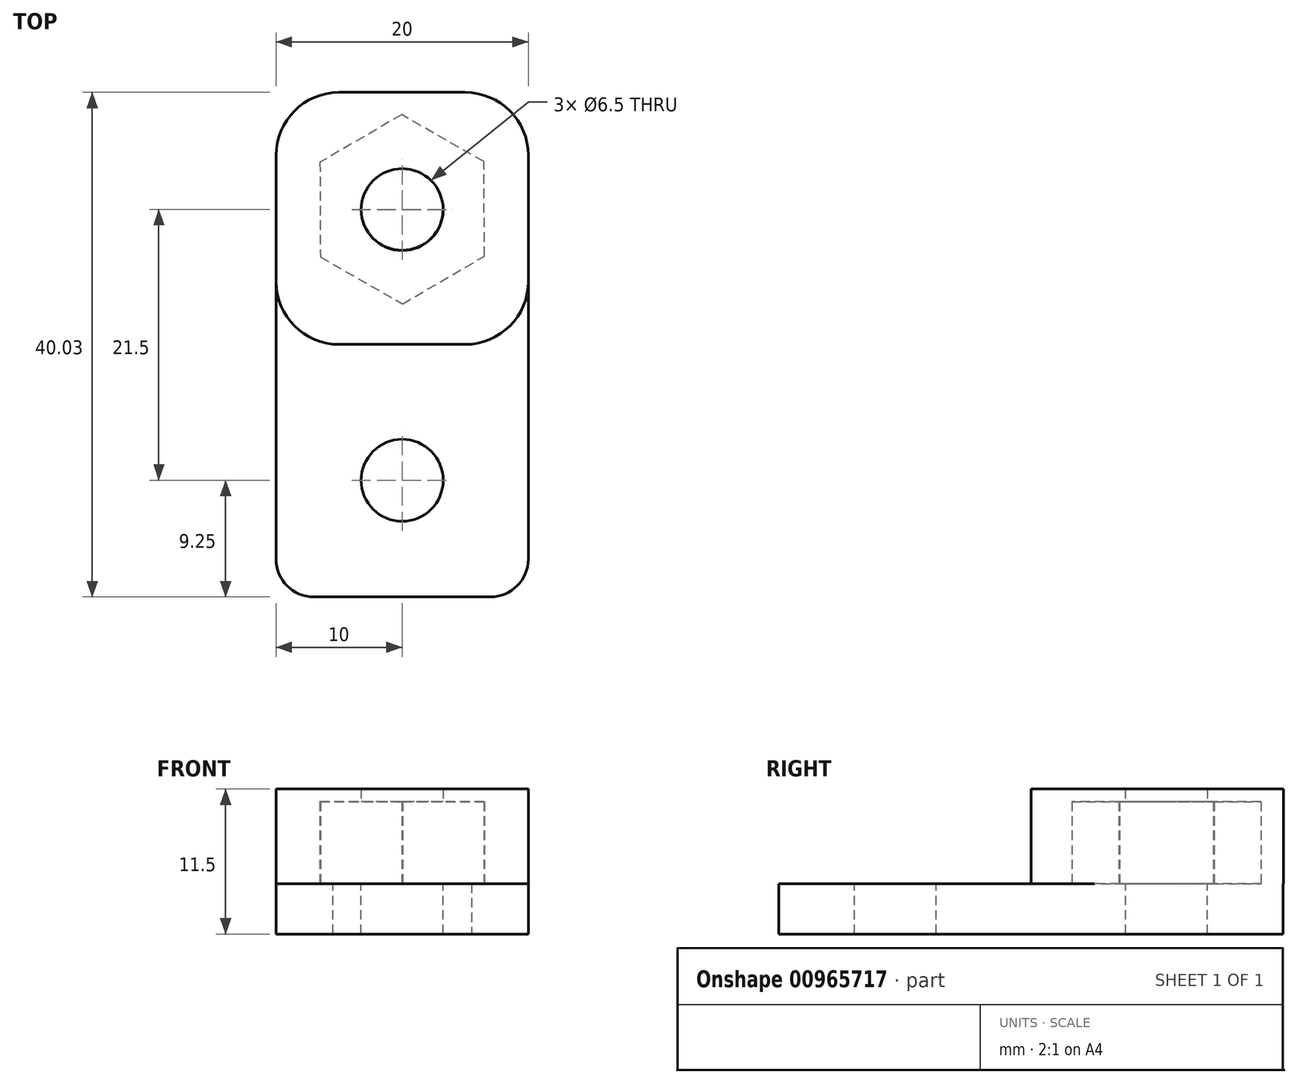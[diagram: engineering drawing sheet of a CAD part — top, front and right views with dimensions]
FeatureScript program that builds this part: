
annotation { "Feature Type Name" : "Feature", "Feature Type Description" : "" }
export const myFeature = defineFeature(function(context is Context, id is Id, definition is map)
    precondition{}
    {
        {
            var Q0;
            Q0=qCreatedBy(makeId("Top.planeOp"),FACE);
            var sketch = newSketch(context, id + "F0", { "sketchPlane" : qUnion([Q0])});
            skLineSegment(sketch, "E0.bottom", {"start": v(0, 0) * mm, "end": v(20, 0) * mm});
            skLineSegment(sketch, "E0.top", {"start": v(0, 40) * mm, "end": v(20, 40) * mm});
            skLineSegment(sketch, "E0.left", {"start": v(0, 0) * mm, "end": v(0, 40) * mm});
            skLineSegment(sketch, "E0.right", {"start": v(20, 0) * mm, "end": v(20, 40) * mm});
            skLineSegment(sketch, "E1.left", {"start": v(0, 40) * mm, "end": v(0, 40) * mm});
            skLineSegment(sketch, "E1.right", {"start": v(20, 40) * mm, "end": v(20, 40) * mm});
            skSolve(sketch);
        }
        {
            var Q0;
            Q0=makeQuery(id+"F0.imprint","IMPRINT",FACE,{"disambiguationData":[TD([[makeQuery(id+"F0.imprint","IMPRINT",EDGE,{"derivedFrom":sQuery(id+"F0.wireOp",EDGE,"E0.bottom")}),1.0]])]});
            extrude(context, id + "F1", {"entities" : qUnion([Q0]), "depth" : 4 * mm, "offsetDistance" : 25 * mm});
        }
        {
            var Q0;
            Q0=makeQuery(id+"F1.opExtrude","SWEPT_EDGE",EDGE,{"disambiguationData":[OSD([sQuery(id+"F0.wireOp",EDGE,"E0.right"),sQuery(id+"F0.wireOp",EDGE,"E0.top")])]});
            var Q1;
            Q1=makeQuery(id+"F1.opExtrude","SWEPT_EDGE",EDGE,{"disambiguationData":[OSD([sQuery(id+"F0.wireOp",EDGE,"E0.bottom"),sQuery(id+"F0.wireOp",EDGE,"E0.right")])]});
            var Q2;
            Q2=makeQuery(id+"F1.opExtrude","SWEPT_EDGE",EDGE,{"disambiguationData":[OSD([sQuery(id+"F0.wireOp",EDGE,"E0.left"),sQuery(id+"F0.wireOp",EDGE,"E0.top")])]});
            var Q3;
            Q3=makeQuery(id+"F1.opExtrude","SWEPT_EDGE",EDGE,{"disambiguationData":[OSD([sQuery(id+"F0.wireOp",EDGE,"E0.bottom"),sQuery(id+"F0.wireOp",EDGE,"E0.left")])]});
            fillet(context, id + "F2", {"entities" : qUnion([Q0, Q1, Q2, Q3]), "radius" : 3 * mm, "tangentPropagation" : true, "allowEdgeOverflow" : false});
        }
        {
            var Q0;
            Q0=makeQuery(id+"F1.opExtrude","CAP_FACE",FACE,{"disambiguationData":[OSD([sQuery(id+"F0.wireOp",EDGE,"E0.bottom"),sQuery(id+"F0.wireOp",EDGE,"E0.left"),sQuery(id+"F0.wireOp",EDGE,"E0.right"),sQuery(id+"F0.wireOp",EDGE,"E0.top")])],"isStart":false});
            var sketch = newSketch(context, id + "F3", { "sketchPlane" : qUnion([Q0])});
            skLineSegment(sketch, "E2", {"start": v(0, 20) * mm, "end": v(20, 20) * mm, "construction": true});
            skCircle(sketch, "E3", {"center": v(10, 30.75) * mm, "radius": 3.25 * mm});
            skPoint(sketch, "E3.centerSnap0", {"position": v(10, 40) * mm});
            skCircle(sketch, "E4", {"center": v(10, 9.25) * mm, "radius": 3.25 * mm});
            skPoint(sketch, "E4.centerSnap0", {"position": v(10, 0) * mm});
            skSolve(sketch);
        }
        {
            var Q0;
            Q0=makeQuery(id+"F3.imprint","IMPRINT",FACE,{"disambiguationData":[TD([[makeQuery(id+"F3.imprint","IMPRINT",EDGE,{"derivedFrom":sQuery(id+"F3.wireOp",EDGE,"E3")}),1.0]])]});
            var Q1;
            Q1=makeQuery(id+"F3.imprint","IMPRINT",FACE,{"disambiguationData":[TD([[makeQuery(id+"F3.imprint","IMPRINT",EDGE,{"derivedFrom":sQuery(id+"F3.wireOp",EDGE,"E4")}),1.0]])]});
            var Q2;
            Q2=sQuery(id+"F3.wireOp",EDGE,"E3");
            var Q3;
            Q3=sQuery(id+"F3.wireOp",EDGE,"E4");
            extrude(context, id + "F4", {"entities" : qUnion([Q0, Q1]), "operationType" : NewBodyOperationType.REMOVE, "surfaceEntities" : qUnion([Q2, Q3]), "endBound" : BoundingType.THROUGH_ALL, "oppositeDirection" : true, "depth" : 4 * mm, "offsetDistance" : 25 * mm});
        }
        {
            var Q0;
            Q0=makeQuery(id+"F1.opExtrude","CAP_FACE",FACE,{"disambiguationData":[OSD([sQuery(id+"F0.wireOp",EDGE,"E0.bottom"),sQuery(id+"F0.wireOp",EDGE,"E0.left"),sQuery(id+"F0.wireOp",EDGE,"E0.right"),sQuery(id+"F0.wireOp",EDGE,"E0.top")])],"isStart":false});
            var sketch = newSketch(context, id + "F5", { "sketchPlane" : qUnion([Q0])});
            skCircle(sketch, "E5.cCircle", {"center": v(10, 30.75) * mm, "radius": 7.5 * mm, "construction": true});
            skLineSegment(sketch, "E5.0", {"start": v(10.03, 23.24) * mm, "end": v(3.52, 26.97) * mm});
            skLineSegment(sketch, "E5.1", {"start": v(3.52, 26.97) * mm, "end": v(3.48, 34.47) * mm});
            skLineSegment(sketch, "E5.2", {"start": v(3.48, 34.47) * mm, "end": v(9.97, 38.26) * mm});
            skLineSegment(sketch, "E5.3", {"start": v(9.97, 38.26) * mm, "end": v(16.48, 34.53) * mm});
            skLineSegment(sketch, "E5.4", {"start": v(16.48, 34.53) * mm, "end": v(16.52, 27.03) * mm});
            skLineSegment(sketch, "E5.5", {"start": v(16.52, 27.03) * mm, "end": v(10.03, 23.24) * mm});
            skSolve(sketch);
        }
        {
            var Q0;
            Q0=makeQuery(id+"F5.imprint","IMPRINT",FACE,{"disambiguationData":[TD([[makeQuery(id+"F5.imprint","IMPRINT",EDGE,{"derivedFrom":sQuery(id+"F5.wireOp",EDGE,"E5.0")}),1.0]])]});
            var sketch = newSketch(context, id + "F6", { "sketchPlane" : qUnion([Q0])});
            skLineSegment(sketch, "E6.bottom", {"start": v(20, 20.03) * mm, "end": v(0, 20.03) * mm});
            skLineSegment(sketch, "E6.top", {"start": v(20, 40.03) * mm, "end": v(0, 40.03) * mm});
            skLineSegment(sketch, "E6.left", {"start": v(20, 20.03) * mm, "end": v(20, 40.03) * mm});
            skLineSegment(sketch, "E6.right", {"start": v(0, 20.03) * mm, "end": v(0, 40.03) * mm});
            skSolve(sketch);
        }
        {
            var Q0;
            Q0=makeQuery(id+"F6.imprint","IMPRINT",FACE,{"disambiguationData":[TD([[makeQuery(id+"F6.imprint","IMPRINT",EDGE,{"derivedFrom":makeQuery(id+"F5.imprint","IMPRINT",EDGE,{"derivedFrom":sQuery(id+"F5.wireOp",EDGE,"E5.0")})}),-1.0]])]});
            var Q1;
            {var subQ6=sQuery(id+"F6.wireOp",EDGE,"E6.top");Q1=makeQuery(id+"F6.imprint","IMPRINT",FACE,{"disambiguationData":[TD([[makeQuery(id+"F6.imprint","IMPRINT",EDGE,{"derivedFrom":subQ6}),1.0]])]});}
            var Q2;
            {var subQ5=sQuery(id+"F6.wireOp",EDGE,"E6.bottom");Q2=makeQuery(id+"F6.imprint","IMPRINT",FACE,{"disambiguationData":[TD([[makeQuery(id+"F6.imprint","IMPRINT",EDGE,{"derivedFrom":subQ5}),-1.0]])]});}
            extrude(context, id + "F7", {"entities" : qUnion([Q0, Q1, Q2]), "operationType" : NewBodyOperationType.ADD, "depth" : 6.5 * mm, "offsetDistance" : 25 * mm});
        }
        {
            var Q0;
            Q0 = qSketchRegion(id + "F5", true);
            var Q1;
            Q1=sQuery(id+"F5.wireOp",EDGE,"E5.0");
            var Q2;
            Q2=sQuery(id+"F5.wireOp",EDGE,"E5.2");
            var Q3;
            Q3=sQuery(id+"F5.wireOp",EDGE,"E5.1");
            var Q4;
            Q4=sQuery(id+"F5.wireOp",EDGE,"E5.3");
            var Q5;
            Q5=sQuery(id+"F5.wireOp",EDGE,"E5.5");
            var Q6;
            Q6=sQuery(id+"F5.wireOp",EDGE,"E5.4");
            extrude(context, id + "F8", {"entities" : qUnion([Q0]), "operationType" : NewBodyOperationType.REMOVE, "surfaceEntities" : qUnion([Q1, Q2, Q3, Q4, Q5, Q6]), "depth" : 6.6 * mm, "offsetDistance" : 25 * mm});
        }
        {
            var Q0;
            Q0=makeQuery(id+"F7.opExtrude","SWEPT_EDGE",EDGE,{"disambiguationData":[OSD([sQuery(id+"F6.wireOp",EDGE,"E6.top"),sQuery(id+"F6.wireOp",EDGE,"E6.left")])]});
            var Q1;
            Q1=makeQuery(id+"F7.opExtrude","SWEPT_EDGE",EDGE,{"disambiguationData":[OSD([sQuery(id+"F6.wireOp",EDGE,"E6.top"),sQuery(id+"F6.wireOp",EDGE,"E6.right")])]});
            fillet(context, id + "F9", {"entities" : qUnion([Q0, Q1]), "radius" : 5 * mm, "tangentPropagation" : true, "allowEdgeOverflow" : false});
        }
        {
            var Q0;
            Q0=makeQuery(id+"F7.opExtrude","SWEPT_EDGE",EDGE,{"disambiguationData":[OSD([sQuery(id+"F0.wireOp",EDGE,"E0.left"),sQuery(id+"F6.wireOp",EDGE,"E6.bottom"),sQuery(id+"F6.wireOp",EDGE,"E6.right")])]});
            var Q1;
            Q1=makeQuery(id+"F7.opExtrude","SWEPT_EDGE",EDGE,{"disambiguationData":[OSD([sQuery(id+"F0.wireOp",EDGE,"E0.right"),sQuery(id+"F6.wireOp",EDGE,"E6.bottom"),sQuery(id+"F6.wireOp",EDGE,"E6.left")])]});
            fillet(context, id + "F10", {"entities" : qUnion([Q0, Q1]), "radius" : 5 * mm, "tangentPropagation" : true, "allowEdgeOverflow" : false});
        }
        {
            var Q0;
            Q0=makeQuery(id+"F7.opExtrude","CAP_FACE",FACE,{"disambiguationData":[OSD([sQuery(id+"F6.wireOp",EDGE,"E6.bottom"),sQuery(id+"F6.wireOp",EDGE,"E6.top"),sQuery(id+"F6.wireOp",EDGE,"E6.left"),sQuery(id+"F6.wireOp",EDGE,"E6.right")])],"isStart":false});
            var sketch = newSketch(context, id + "F11", { "sketchPlane" : qUnion([Q0])});
            skPoint(sketch, "E7.firstSnap0", {"position": v(0, 30.03) * mm});
            skLineSegment(sketch, "E7.bottom", {"start": v(0, 40.03) * mm, "end": v(20, 40.03) * mm});
            skLineSegment(sketch, "E7.top", {"start": v(0, 20.03) * mm, "end": v(20, 20.03) * mm});
            skLineSegment(sketch, "E7.left", {"start": v(0, 40.03) * mm, "end": v(0, 20.03) * mm});
            skLineSegment(sketch, "E7.right", {"start": v(20, 40.03) * mm, "end": v(20, 20.03) * mm});
            skCircle(sketch, "E8", {"center": v(10, 30.72) * mm, "radius": 3.25 * mm});
            skPoint(sketch, "E8.centerSnap0", {"position": v(10, 40.03) * mm});
            skPoint(sketch, "E8.centerSnap1", {"position": v(3.5, 30.72) * mm});
            skSolve(sketch);
        }
        {
            var Q0;
            {var subQ0=sQuery(id+"F6.wireOp",EDGE,"E6.right");var subQ1=sQuery(id+"F6.wireOp",EDGE,"E6.left");var subQ2=sQuery(id+"F6.wireOp",EDGE,"E6.top");var subQ3=sQuery(id+"F6.wireOp",EDGE,"E6.bottom");var subQ4=makeQuery(id+"F7.opExtrude","CAP_FACE",FACE,{"disambiguationData":[OSD([subQ3,subQ2,subQ1,subQ0])],"isStart":false});Q0=makeQuery(id+"F11.imprint","IMPRINT",FACE,{"disambiguationData":[TD([[makeQuery(id+"F11.imprint","IMPRINT",EDGE,{"derivedFrom":makeQuery(id+"F8.boolean.opBoolean","INTERSECT",EDGE,{"derivedFrom":[subQ4,makeQuery(id+"F8.opExtrude","SWEPT_FACE",FACE,{"disambiguationData":[OSD([sQuery(id+"F5.wireOp",EDGE,"E5.0")])]})]})}),-1.0]])]});}
            var Q1;
            Q1 = qSketchRegion(id + "F11", true);
            extrude(context, id + "F12", {"entities" : qUnion([Q0, Q1]), "operationType" : NewBodyOperationType.ADD, "depth" : 1 * mm, "offsetDistance" : 25 * mm});
        }
        {
            var Q0;
            Q0=makeQuery(id+"F12.opExtrude","SWEPT_EDGE",EDGE,{"disambiguationData":[OSD([sQuery(id+"F11.wireOp",EDGE,"E7.bottom"),sQuery(id+"F11.wireOp",EDGE,"E7.left")])]});
            var Q1;
            Q1=makeQuery(id+"F12.opExtrude","SWEPT_EDGE",EDGE,{"disambiguationData":[OSD([sQuery(id+"F11.wireOp",EDGE,"E7.top"),sQuery(id+"F11.wireOp",EDGE,"E7.right")])]});
            var Q2;
            Q2=makeQuery(id+"F12.opExtrude","SWEPT_EDGE",EDGE,{"disambiguationData":[OSD([sQuery(id+"F11.wireOp",EDGE,"E7.bottom"),sQuery(id+"F11.wireOp",EDGE,"E7.right")])]});
            var Q3;
            Q3=makeQuery(id+"F12.opExtrude","SWEPT_EDGE",EDGE,{"disambiguationData":[OSD([sQuery(id+"F11.wireOp",EDGE,"E7.top"),sQuery(id+"F11.wireOp",EDGE,"E7.left")])]});
            fillet(context, id + "F13", {"entities" : qUnion([Q0, Q1, Q2, Q3]), "radius" : 5 * mm, "tangentPropagation" : true, "allowEdgeOverflow" : false});
        }
    });
